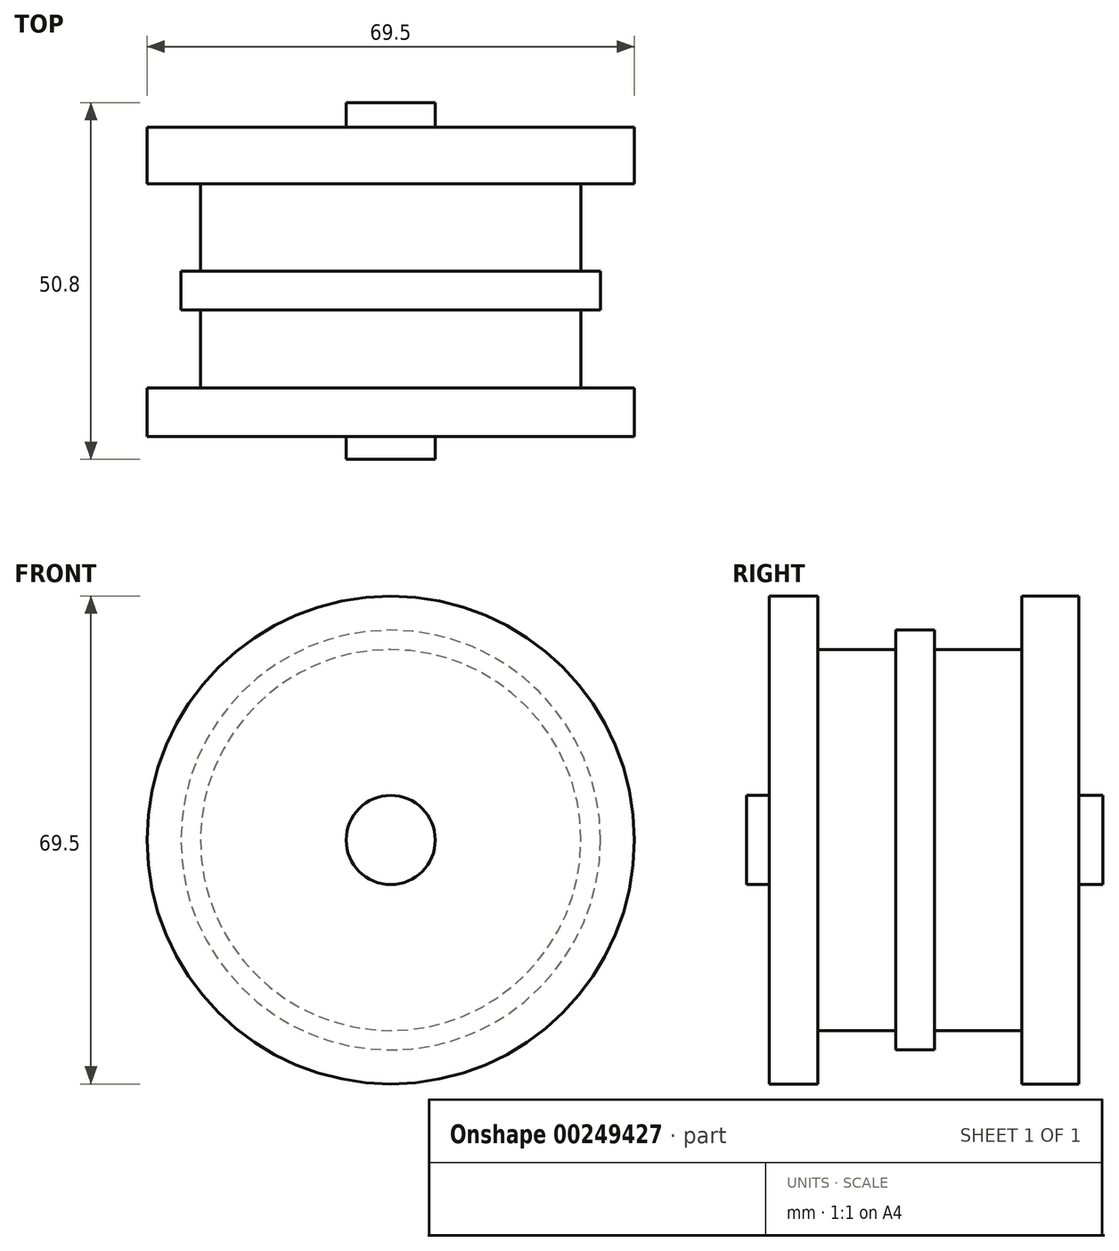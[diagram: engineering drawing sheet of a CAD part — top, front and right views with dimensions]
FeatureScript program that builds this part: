
annotation { "Feature Type Name" : "Feature", "Feature Type Description" : "" }
export const myFeature = defineFeature(function(context is Context, id is Id, definition is map)
    precondition{}
    {
        {
            var Q0;
            Q0=qCreatedBy(makeId("Front.planeOp"),FACE);
            var sketch = newSketch(context, id + "F0", { "sketchPlane" : qUnion([Q0])});
            skCircle(sketch, "E0", {"center": v(0, 0) * mm, "radius": 6.35 * mm});
            skSolve(sketch);
        }
        {
            var Q0;
            Q0=makeQuery(id+"F0.imprint","IMPRINT",FACE,{"disambiguationData":[TD([[makeQuery(id+"F0.imprint","IMPRINT",EDGE,{"derivedFrom":sQuery(id+"F0.wireOp",EDGE,"E0")}),1.0]])]});
            extrude(context, id + "F1", {"entities" : qUnion([Q0]), "depth" : 50.8 * mm});
        }
        {
            var Q0;
            Q0=qCreatedBy(makeId("Right.planeOp"),FACE);
            var sketch = newSketch(context, id + "F2", { "sketchPlane" : qUnion([Q0])});
            skLineSegment(sketch, "E1.bottom", {"start": v(-3.46, 0) * mm, "end": v(-11.55, 0) * mm});
            skLineSegment(sketch, "E1.top", {"start": v(-3.46, 34.75) * mm, "end": v(-11.55, 34.75) * mm});
            skLineSegment(sketch, "E1.left", {"start": v(-3.46, 0) * mm, "end": v(-3.46, 34.75) * mm});
            skLineSegment(sketch, "E1.right", {"start": v(-11.55, 27.13) * mm, "end": v(-11.55, 34.75) * mm});
            skLineSegment(sketch, "E2.bottom", {"start": v(-11.55, 27.13) * mm, "end": v(-24.01, 27.13) * mm});
            skLineSegment(sketch, "E2.top", {"start": v(-11.55, 0) * mm, "end": v(-47.57, 0) * mm});
            skLineSegment(sketch, "E2.right", {"start": v(-47.57, 27.13) * mm, "end": v(-47.57, 0) * mm});
            skLineSegment(sketch, "E3.bottom", {"start": v(-47.57, 0) * mm, "end": v(-40.64, 0) * mm});
            skLineSegment(sketch, "E3.top", {"start": v(-47.57, 34.75) * mm, "end": v(-40.64, 34.75) * mm});
            skLineSegment(sketch, "E3.left", {"start": v(-47.57, 0) * mm, "end": v(-47.57, 34.75) * mm});
            skLineSegment(sketch, "E3.right", {"start": v(-40.64, 27.13) * mm, "end": v(-40.64, 34.75) * mm});
            skPoint(sketch, "E4.oppositeSnap0", {"position": v(-29.56, 27.13) * mm});
            skLineSegment(sketch, "E4.top", {"start": v(-24.01, 29.9) * mm, "end": v(-29.56, 29.9) * mm});
            skLineSegment(sketch, "E4.left", {"start": v(-24.01, 27.13) * mm, "end": v(-24.01, 29.9) * mm});
            skLineSegment(sketch, "E4.right", {"start": v(-29.56, 27.13) * mm, "end": v(-29.56, 29.9) * mm});
            skLineSegment(sketch, "E5.trimOffspring", {"start": v(-29.56, 27.13) * mm, "end": v(-40.64, 27.13) * mm});
            skSolve(sketch);
        }
        {
            var Q0;
            Q0=makeQuery(id+"F2.imprint","IMPRINT",FACE,{"disambiguationData":[TD([[makeQuery(id+"F2.imprint","IMPRINT",EDGE,{"derivedFrom":sQuery(id+"F2.wireOp",EDGE,"E1.bottom")}),-1.0]])]});
            var Q1;
            Q1=sQuery(id+"F2.wireOp",EDGE,"E2.top");
            revolve(context, id + "F3", {"operationType" : NewBodyOperationType.ADD, "entities" : qUnion([Q0]), "axis" : qUnion([Q1]), "revolveType" : RevolveType.FULL});
        }
    });
